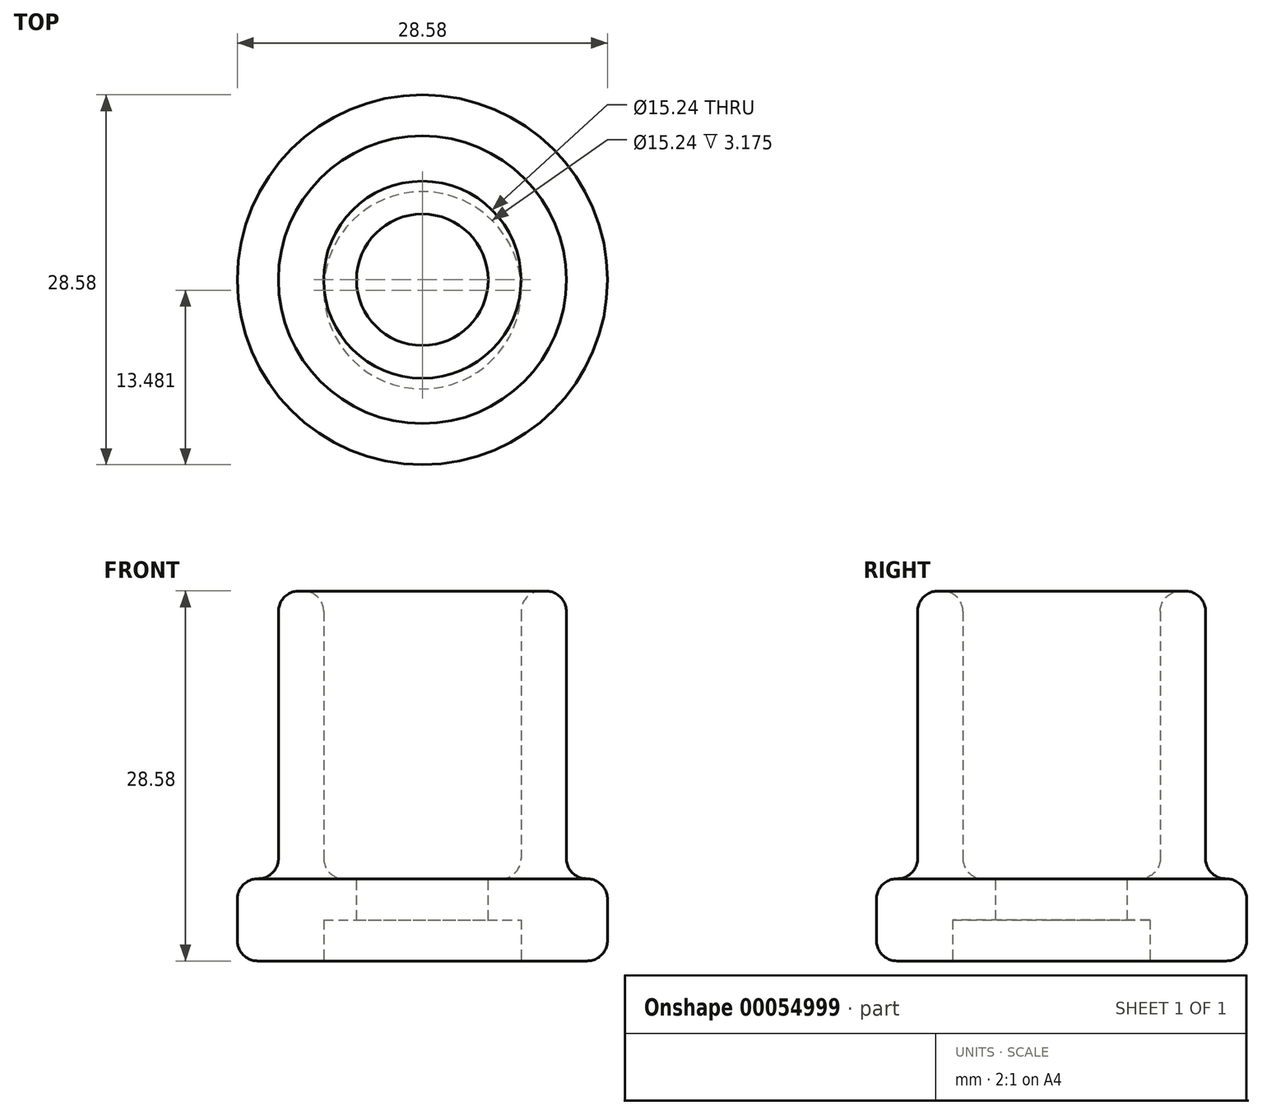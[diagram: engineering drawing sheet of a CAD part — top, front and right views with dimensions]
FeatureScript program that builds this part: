
annotation { "Feature Type Name" : "Feature", "Feature Type Description" : "" }
export const myFeature = defineFeature(function(context is Context, id is Id, definition is map)
    precondition{}
    {
        {
            var Q0;
            Q0=qCreatedBy(makeId("Top.planeOp"),FACE);
            var sketch = newSketch(context, id + "F0", { "sketchPlane" : qUnion([Q0])});
            skCircle(sketch, "E0", {"center": v(0, 0) * mm, "radius": 7.62 * mm});
            skCircle(sketch, "E1", {"center": v(0, 0) * mm, "radius": 11.11 * mm});
            skCircle(sketch, "E2", {"center": v(0, 0) * mm, "radius": 14.29 * mm});
            skCircle(sketch, "E3", {"center": v(0, 0) * mm, "radius": 5.08 * mm});
            skSolve(sketch);
        }
        {
            var Q0;
            Q0=makeQuery(id+"F0.imprint","IMPRINT",FACE,{"disambiguationData":[TD([[makeQuery(id+"F0.imprint","IMPRINT",EDGE,{"derivedFrom":sQuery(id+"F0.wireOp",EDGE,"E0")}),-1.0]])]});
            extrude(context, id + "F1", {"entities" : qUnion([Q0]), "depth" : 22.22 * mm});
        }
        {
            var Q0;
            Q0=makeQuery(id+"F0.imprint","IMPRINT",FACE,{"disambiguationData":[TD([[makeQuery(id+"F0.imprint","IMPRINT",EDGE,{"derivedFrom":sQuery(id+"F0.wireOp",EDGE,"E1")}),-1.0]])]});
            var Q1;
            Q1=makeQuery(id+"F0.imprint","IMPRINT",FACE,{"disambiguationData":[TD([[makeQuery(id+"F0.imprint","IMPRINT",EDGE,{"derivedFrom":sQuery(id+"F0.wireOp",EDGE,"E0")}),-1.0]])]});
            var Q2;
            Q2=makeQuery(id+"F0.imprint","IMPRINT",FACE,{"disambiguationData":[TD([[makeQuery(id+"F0.imprint","IMPRINT",EDGE,{"derivedFrom":sQuery(id+"F0.wireOp",EDGE,"E0")}),1.0]])]});
            extrude(context, id + "F2", {"entities" : qUnion([Q0, Q1, Q2]), "operationType" : NewBodyOperationType.ADD, "oppositeDirection" : true, "depth" : 6.35 * mm});
        }
        {
            var Q0;
            Q0=makeQuery(id+"F2.opExtrude","CAP_FACE",FACE,{"disambiguationData":[OSD([sQuery(id+"F0.wireOp",EDGE,"E2"),sQuery(id+"F0.wireOp",EDGE,"E3")])],"isStart":false});
            var sketch = newSketch(context, id + "F3", { "sketchPlane" : qUnion([Q0])});
            skCircle(sketch, "E4", {"center": v(0, 0.8) * mm, "radius": 7.62 * mm});
            skSolve(sketch);
        }
        {
            var Q0;
            Q0 = qSketchRegion(id + "F3", true);
            extrude(context, id + "F4", {"entities" : qUnion([Q0]), "operationType" : NewBodyOperationType.REMOVE, "oppositeDirection" : true, "depth" : 3.17 * mm});
        }
        {
            var Q0;
            Q0=makeQuery(id+"F1.opExtrude","SWEPT_FACE",FACE,{"disambiguationData":[OSD([sQuery(id+"F0.wireOp",EDGE,"E0")])]});
            var Q1;
            Q1=makeQuery(id+"F1.opExtrude","SWEPT_FACE",FACE,{"disambiguationData":[OSD([sQuery(id+"F0.wireOp",EDGE,"E1")])]});
            var Q2;
            Q2=makeQuery(id+"F2.opExtrude","SWEPT_FACE",FACE,{"disambiguationData":[OSD([sQuery(id+"F0.wireOp",EDGE,"E2")])]});
            var Q3;
            Q3=makeQuery(id+"F4.boolean.opBoolean","COPY",EDGE,{"derivedFrom":makeQuery(id+"F4.opExtrude","CAP_EDGE",EDGE,{"disambiguationData":[OSD([sQuery(id+"F3.wireOp",EDGE,"E4")])],"isStart":true})});
            fillet(context, id + "F5", {"entities" : qUnion([Q0, Q1, Q2, Q3]), "radius" : 1.57 * mm, "tangentPropagation" : true, "allowEdgeOverflow" : false});
        }
    });
